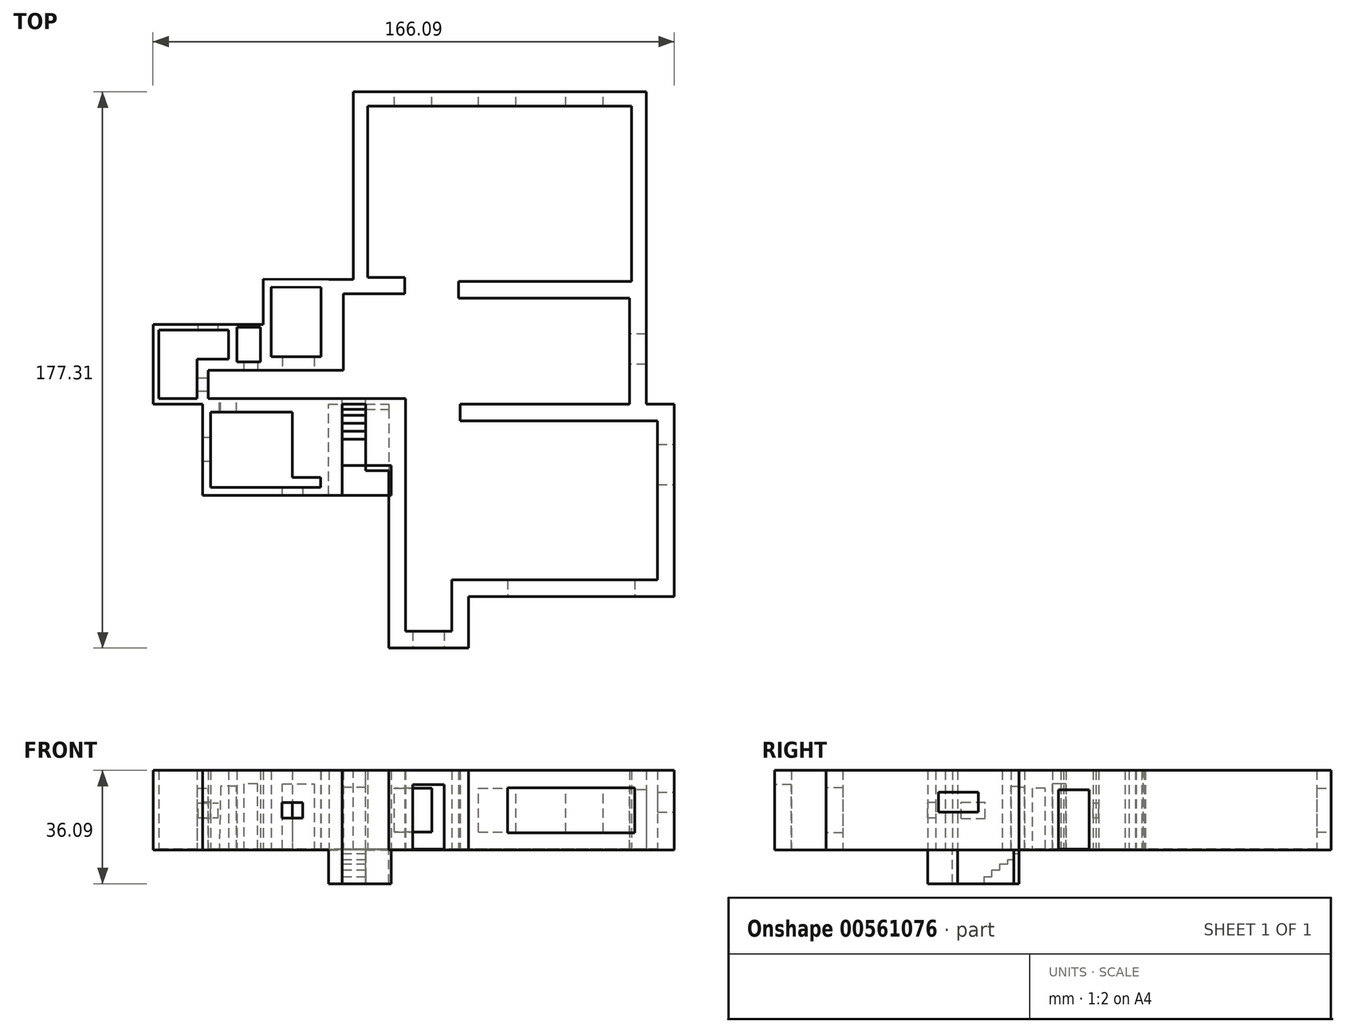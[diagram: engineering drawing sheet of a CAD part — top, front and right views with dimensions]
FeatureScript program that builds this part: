
annotation { "Feature Type Name" : "Feature", "Feature Type Description" : "" }
export const myFeature = defineFeature(function(context is Context, id is Id, definition is map)
    precondition{}
    {
        {
            var Q0;
            Q0=qCreatedBy(makeId("Top.planeOp"),FACE);
            var sketch = newSketch(context, id + "F0", { "sketchPlane" : qUnion([Q0])});
            skLineSegment(sketch, "E0", {"start": v(7.67, -76.15) * mm, "end": v(7.67, -59.75) * mm});
            skLineSegment(sketch, "E1", {"start": v(7.67, -59.75) * mm, "end": v(73.28, -59.75) * mm});
            skLineSegment(sketch, "E2", {"start": v(73.28, -59.75) * mm, "end": v(73.28, 1.64) * mm});
            skLineSegment(sketch, "E3", {"start": v(73.28, 1.64) * mm, "end": v(5.02, 1.64) * mm});
            skLineSegment(sketch, "E4", {"start": v(64.29, 9.05) * mm, "end": v(64.29, 21.75) * mm});
            skLineSegment(sketch, "E5", {"start": v(64.29, 21.75) * mm, "end": v(64.29, 30.21) * mm});
            skLineSegment(sketch, "E6", {"start": v(64.29, 30.21) * mm, "end": v(64.29, 40.8) * mm});
            skLineSegment(sketch, "E7", {"start": v(64.29, 40.8) * mm, "end": v(4.5, 40.8) * mm});
            skLineSegment(sketch, "E8", {"start": v(64.29, 51.38) * mm, "end": v(64.29, 56.89) * mm});
            skLineSegment(sketch, "E9", {"start": v(64.29, 56.89) * mm, "end": v(64.29, 101.16) * mm});
            skLineSegment(sketch, "E10", {"start": v(64.29, 101.16) * mm, "end": v(-28.95, 101.16) * mm});
            skLineSegment(sketch, "E11", {"start": v(-28.95, 101.16) * mm, "end": v(-28.95, 52.66) * mm});
            skLineSegment(sketch, "E12", {"start": v(-28.95, 52.66) * mm, "end": v(-17.16, 52.66) * mm});
            skLineSegment(sketch, "E13", {"start": v(-17.16, 52.66) * mm, "end": v(-17.16, 41.31) * mm});
            skLineSegment(sketch, "E14", {"start": v(-17.16, 41.31) * mm, "end": v(-36.74, 41.31) * mm});
            skLineSegment(sketch, "E15", {"start": v(-36.74, 41.31) * mm, "end": v(-36.74, 14.17) * mm});
            skLineSegment(sketch, "E16", {"start": v(-36.74, 14.17) * mm, "end": v(-42.75, 14.17) * mm});
            skLineSegment(sketch, "E17", {"start": v(-50.53, 14.17) * mm, "end": v(-57.65, 14.17) * mm});
            skLineSegment(sketch, "E18", {"start": v(-57.65, 14.17) * mm, "end": v(-57.65, 27.07) * mm});
            skLineSegment(sketch, "E19", {"start": v(-57.65, 41.54) * mm, "end": v(-36.74, 41.31) * mm});
            skLineSegment(sketch, "E20", {"start": v(-67, 14.17) * mm, "end": v(-67, 27.07) * mm});
            skLineSegment(sketch, "E21", {"start": v(-67, 27.07) * mm, "end": v(-57.65, 27.07) * mm});
            skPoint(sketch, "E22.start.orphan", {"position": v(-17.73, -76.15) * mm});
            skLineSegment(sketch, "E23", {"start": v(-17.73, -76.15) * mm, "end": v(-17.73, 1.64) * mm});
            skLineSegment(sketch, "E24", {"start": v(-17.73, 1.64) * mm, "end": v(-30.5, 1.64) * mm});
            skLineSegment(sketch, "E25", {"start": v(-39.19, 1.64) * mm, "end": v(-45.86, 1.64) * mm});
            skLineSegment(sketch, "E26", {"start": v(-45.86, -27.43) * mm, "end": v(-77, -27.43) * mm});
            skLineSegment(sketch, "E27", {"start": v(-77, -27.43) * mm, "end": v(-77, 1.64) * mm});
            skLineSegment(sketch, "E28", {"start": v(-77, 1.64) * mm, "end": v(-51.87, 1.64) * mm});
            skLineSegment(sketch, "E29", {"start": v(-77, 14.17) * mm, "end": v(-67, 14.17) * mm});
            skLineSegment(sketch, "E30", {"start": v(-77, 1.64) * mm, "end": v(-92.8, 1.64) * mm});
            skLineSegment(sketch, "E31", {"start": v(-92.8, 1.64) * mm, "end": v(-92.8, 27.07) * mm});
            skLineSegment(sketch, "E32", {"start": v(-77, 27.07) * mm, "end": v(-67, 27.07) * mm});
            skLineSegment(sketch, "E33", {"start": v(-77, 1.64) * mm, "end": v(-77, 8.77) * mm});
            skLineSegment(sketch, "E34", {"start": v(-45.86, -19.24) * mm, "end": v(-45.86, 1.64) * mm});
            skLineSegment(sketch, "E35", {"start": v(-45.86, -27.43) * mm, "end": v(-36.9, -27.43) * mm});
            skLineSegment(sketch, "E36", {"start": v(-36.9, -27.43) * mm, "end": v(-36.9, -19.24) * mm});
            skLineSegment(sketch, "E37", {"start": v(-36.9, -19.24) * mm, "end": v(-45.86, -19.24) * mm});
            skLineSegment(sketch, "E38", {"start": v(-67, 14.17) * mm, "end": v(-57.65, 14.17) * mm});
            skLineSegment(sketch, "E39", {"start": v(-77, 8.77) * mm, "end": v(-77, 14.17) * mm});
            skLineSegment(sketch, "E40", {"start": v(-51.87, 1.64) * mm, "end": v(-45.86, 1.64) * mm});
            skLineSegment(sketch, "E41", {"start": v(-50.53, 14.17) * mm, "end": v(-42.75, 14.17) * mm});
            skLineSegment(sketch, "E42", {"start": v(-39.19, 1.64) * mm, "end": v(-30.5, 1.64) * mm});
            skLineSegment(sketch, "E43", {"start": v(-17.73, -76.15) * mm, "end": v(7.67, -76.15) * mm});
            skLineSegment(sketch, "E44", {"start": v(64.29, 9.05) * mm, "end": v(64.29, 1.64) * mm});
            skLineSegment(sketch, "E45", {"start": v(64.29, 51.38) * mm, "end": v(64.29, 40.8) * mm});
            skLineSegment(sketch, "E46.0", {"start": v(67.95, -3.7) * mm, "end": v(5.02, -3.7) * mm});
            skLineSegment(sketch, "E46.1", {"start": v(67.95, -54.41) * mm, "end": v(67.95, -3.7) * mm});
            skLineSegment(sketch, "E46.2", {"start": v(2.33, -54.41) * mm, "end": v(67.95, -54.41) * mm});
            skLineSegment(sketch, "E46.3", {"start": v(2.33, -76.15) * mm, "end": v(2.33, -54.41) * mm});
            skLineSegment(sketch, "E47", {"start": v(5.02, -3.7) * mm, "end": v(5.02, 1.64) * mm});
            skLineSegment(sketch, "E48.0", {"start": v(58.95, 35.46) * mm, "end": v(4.5, 35.46) * mm});
            skLineSegment(sketch, "E48.1", {"start": v(58.95, 9.05) * mm, "end": v(58.95, 1.64) * mm});
            skLineSegment(sketch, "E48.2", {"start": v(58.95, 9.05) * mm, "end": v(58.95, 21.75) * mm});
            skLineSegment(sketch, "E48.3", {"start": v(58.95, 21.75) * mm, "end": v(58.95, 30.21) * mm});
            skLineSegment(sketch, "E48.4", {"start": v(58.95, 30.21) * mm, "end": v(58.95, 35.46) * mm});
            skLineSegment(sketch, "E49", {"start": v(4.5, 35.46) * mm, "end": v(4.5, 40.8) * mm});
            skLineSegment(sketch, "E50.0", {"start": v(59.72, 51.38) * mm, "end": v(59.72, 40.8) * mm});
            skLineSegment(sketch, "E50.1", {"start": v(59.72, 51.38) * mm, "end": v(59.72, 56.89) * mm});
            skLineSegment(sketch, "E50.2", {"start": v(59.72, 56.89) * mm, "end": v(59.72, 96.6) * mm});
            skLineSegment(sketch, "E50.3", {"start": v(59.72, 96.6) * mm, "end": v(-24.38, 96.6) * mm});
            skLineSegment(sketch, "E50.4", {"start": v(-24.38, 96.6) * mm, "end": v(-24.38, 57.23) * mm});
            skLineSegment(sketch, "E50.5", {"start": v(-32.17, 36.74) * mm, "end": v(-32.17, 14.17) * mm});
            skLineSegment(sketch, "E50.6", {"start": v(-12.59, 36.74) * mm, "end": v(-32.17, 36.74) * mm});
            skLineSegment(sketch, "E50.7", {"start": v(-12.59, 57.23) * mm, "end": v(-12.59, 36.74) * mm});
            skLineSegment(sketch, "E50.8", {"start": v(-24.38, 57.23) * mm, "end": v(-12.59, 57.23) * mm});
            skLineSegment(sketch, "E51", {"start": v(-32.17, 14.17) * mm, "end": v(-36.74, 14.17) * mm});
            skLineSegment(sketch, "E52.0", {"start": v(-50.53, 16.71) * mm, "end": v(-55.11, 16.71) * mm});
            skLineSegment(sketch, "E52.1", {"start": v(-55.11, 38.97) * mm, "end": v(-39.28, 38.8) * mm});
            skLineSegment(sketch, "E52.2", {"start": v(-39.28, 38.8) * mm, "end": v(-39.28, 16.71) * mm});
            skLineSegment(sketch, "E52.3", {"start": v(-55.11, 16.71) * mm, "end": v(-55.11, 38.97) * mm});
            skLineSegment(sketch, "E52.4", {"start": v(-39.28, 16.71) * mm, "end": v(-42.75, 16.71) * mm});
            skLineSegment(sketch, "E52.5", {"start": v(-50.53, 16.71) * mm, "end": v(-42.75, 16.71) * mm});
            skLineSegment(sketch, "E53.0", {"start": v(-66.1, 26.19) * mm, "end": v(-58.54, 26.19) * mm});
            skLineSegment(sketch, "E53.1", {"start": v(-66.1, 15.06) * mm, "end": v(-66.1, 26.19) * mm});
            skLineSegment(sketch, "E53.2", {"start": v(-66.1, 15.06) * mm, "end": v(-58.54, 15.06) * mm});
            skLineSegment(sketch, "E53.3", {"start": v(-58.54, 15.06) * mm, "end": v(-58.54, 26.19) * mm});
            skLineSegment(sketch, "E54", {"start": v(-92.8, 27.07) * mm, "end": v(-77, 27.07) * mm});
            skLineSegment(sketch, "E55.0", {"start": v(-78.79, 8.77) * mm, "end": v(-78.79, 15.95) * mm});
            skLineSegment(sketch, "E55.1", {"start": v(-78.79, 3.41) * mm, "end": v(-78.79, 8.77) * mm});
            skLineSegment(sketch, "E55.2", {"start": v(-78.79, 15.95) * mm, "end": v(-68.77, 15.95) * mm});
            skLineSegment(sketch, "E55.3", {"start": v(-78.79, 3.41) * mm, "end": v(-91.03, 3.41) * mm});
            skLineSegment(sketch, "E55.4", {"start": v(-68.77, 15.95) * mm, "end": v(-68.77, 25.3) * mm});
            skLineSegment(sketch, "E55.5", {"start": v(-77, 25.3) * mm, "end": v(-68.77, 25.3) * mm});
            skLineSegment(sketch, "E55.6", {"start": v(-91.03, 25.3) * mm, "end": v(-77, 25.3) * mm});
            skLineSegment(sketch, "E55.7", {"start": v(-91.03, 3.41) * mm, "end": v(-91.03, 25.3) * mm});
            skLineSegment(sketch, "E56.0", {"start": v(-17.73, 3.41) * mm, "end": v(-30.5, 3.41) * mm});
            skLineSegment(sketch, "E56.1", {"start": v(-39.19, 3.41) * mm, "end": v(-30.5, 3.41) * mm});
            skLineSegment(sketch, "E56.2", {"start": v(-39.19, 3.41) * mm, "end": v(-45.86, 3.41) * mm});
            skLineSegment(sketch, "E56.3", {"start": v(-50.53, 12.4) * mm, "end": v(-57.65, 12.4) * mm});
            skLineSegment(sketch, "E56.4", {"start": v(-50.53, 12.4) * mm, "end": v(-42.75, 12.4) * mm});
            skLineSegment(sketch, "E56.5", {"start": v(-36.74, 12.4) * mm, "end": v(-42.75, 12.4) * mm});
            skLineSegment(sketch, "E56.6", {"start": v(-32.17, 12.4) * mm, "end": v(-36.74, 12.4) * mm});
            skLineSegment(sketch, "E56.7", {"start": v(-67, 12.4) * mm, "end": v(-57.65, 12.4) * mm});
            skLineSegment(sketch, "E56.8", {"start": v(-75.23, 12.4) * mm, "end": v(-67, 12.4) * mm});
            skLineSegment(sketch, "E56.9", {"start": v(-75.23, 8.77) * mm, "end": v(-75.23, 12.4) * mm});
            skLineSegment(sketch, "E56.10", {"start": v(-75.23, 3.41) * mm, "end": v(-75.23, 8.77) * mm});
            skLineSegment(sketch, "E56.11", {"start": v(-75.23, 3.41) * mm, "end": v(-51.87, 3.41) * mm});
            skLineSegment(sketch, "E56.12", {"start": v(-51.87, 3.41) * mm, "end": v(-45.86, 3.41) * mm});
            skLineSegment(sketch, "E57", {"start": v(-17.73, 1.64) * mm, "end": v(-17.73, 3.41) * mm});
            skLineSegment(sketch, "E58.0", {"start": v(-39.43, -21.78) * mm, "end": v(-48.4, -21.78) * mm});
            skLineSegment(sketch, "E58.1", {"start": v(-39.43, -24.9) * mm, "end": v(-39.43, -21.78) * mm});
            skLineSegment(sketch, "E58.2", {"start": v(-48.4, -21.78) * mm, "end": v(-48.4, -0.9) * mm});
            skLineSegment(sketch, "E58.3", {"start": v(-45.86, -24.9) * mm, "end": v(-39.43, -24.9) * mm});
            skLineSegment(sketch, "E58.4", {"start": v(-51.87, -0.9) * mm, "end": v(-48.4, -0.9) * mm});
            skLineSegment(sketch, "E58.5", {"start": v(-74.47, -0.9) * mm, "end": v(-51.87, -0.9) * mm});
            skLineSegment(sketch, "E58.6", {"start": v(-74.47, -24.9) * mm, "end": v(-74.47, -0.9) * mm});
            skLineSegment(sketch, "E58.7", {"start": v(-45.86, -24.9) * mm, "end": v(-74.47, -24.9) * mm});
            skLineSegment(sketch, "E59", {"start": v(-57.65, 41.54) * mm, "end": v(-57.65, 27.07) * mm});
            skLineSegment(sketch, "E60", {"start": v(-32.17, 12.4) * mm, "end": v(-32.17, 14.17) * mm});
            skLineSegment(sketch, "E61.0", {"start": v(-12.4, -76.15) * mm, "end": v(-12.4, 1.64) * mm});
            skLineSegment(sketch, "E62", {"start": v(-12.4, 1.64) * mm, "end": v(-17.73, 1.64) * mm});
            skLineSegment(sketch, "E63", {"start": v(-17.73, 3.41) * mm, "end": v(-12.4, 3.41) * mm});
            skLineSegment(sketch, "E64", {"start": v(-12.4, 3.41) * mm, "end": v(-12.4, 1.64) * mm});
            skLineSegment(sketch, "E65.0", {"start": v(-17.73, -70.82) * mm, "end": v(7.67, -70.82) * mm});
            skSolve(sketch);
        }
        {
            var Q0;
            {var subQ4=sQuery(id+"F0.wireOp",EDGE,"E0");Q0=makeQuery(id+"F0.imprint","IMPRINT",FACE,{"disambiguationData":[TD([[makeQuery(id+"F0.imprint","IMPRINT",EDGE,{"derivedFrom":subQ4}),1.0]])]});}
            var Q1;
            {var subQ0=sQuery(id+"F0.wireOp",EDGE,"E23");Q1=makeQuery(id+"F0.imprint","IMPRINT",FACE,{"disambiguationData":[TD([[makeQuery(id+"F0.imprint","IMPRINT",EDGE,{"derivedFrom":subQ0}),-1.0]])]});}
            var Q2;
            Q2=makeQuery(id+"F0.imprint","IMPRINT",FACE,{"disambiguationData":[TD([[makeQuery(id+"F0.imprint","IMPRINT",EDGE,{"derivedFrom":sQuery(id+"F0.wireOp",EDGE,"E26")}),-1.0]])]});
            var Q3;
            Q3=makeQuery(id+"F0.imprint","IMPRINT",FACE,{"disambiguationData":[TD([[makeQuery(id+"F0.imprint","IMPRINT",EDGE,{"derivedFrom":sQuery(id+"F0.wireOp",EDGE,"E4")}),1.0]])]});
            var Q4;
            Q4=makeQuery(id+"F0.imprint","IMPRINT",FACE,{"disambiguationData":[TD([[makeQuery(id+"F0.imprint","IMPRINT",EDGE,{"derivedFrom":sQuery(id+"F0.wireOp",EDGE,"E20")}),1.0]])]});
            var Q5;
            Q5=makeQuery(id+"F0.imprint","IMPRINT",FACE,{"disambiguationData":[TD([[makeQuery(id+"F0.imprint","IMPRINT",EDGE,{"derivedFrom":sQuery(id+"F0.wireOp",EDGE,"E57")}),-1.0]])]});
            var Q6;
            Q6=makeQuery(id+"F0.imprint","IMPRINT",FACE,{"disambiguationData":[TD([[makeQuery(id+"F0.imprint","IMPRINT",EDGE,{"derivedFrom":sQuery(id+"F0.wireOp",EDGE,"E8")}),1.0]])]});
            var Q7;
            Q7=makeQuery(id+"F0.imprint","IMPRINT",FACE,{"disambiguationData":[TD([[makeQuery(id+"F0.imprint","IMPRINT",EDGE,{"derivedFrom":sQuery(id+"F0.wireOp",EDGE,"E15")}),-1.0]])]});
            var Q8;
            Q8=makeQuery(id+"F0.imprint","IMPRINT",FACE,{"disambiguationData":[TD([[makeQuery(id+"F0.imprint","IMPRINT",EDGE,{"derivedFrom":sQuery(id+"F0.wireOp",EDGE,"E18")}),1.0]])]});
            var Q9;
            Q9=makeQuery(id+"F0.imprint","IMPRINT",FACE,{"disambiguationData":[TD([[makeQuery(id+"F0.imprint","IMPRINT",EDGE,{"derivedFrom":sQuery(id+"F0.wireOp",EDGE,"E16")}),1.0]])]});
            var Q10;
            {var subQ8=sQuery(id+"F0.wireOp",EDGE,"E1");Q10=makeQuery(id+"F0.imprint","IMPRINT",FACE,{"disambiguationData":[TD([[makeQuery(id+"F0.imprint","IMPRINT",EDGE,{"derivedFrom":subQ8}),1.0]])]});}
            var Q11;
            {var subQ0=sQuery(id+"F0.wireOp",EDGE,"E46.3");var subQ1=sQuery(id+"F0.wireOp",EDGE,"E43");var subQ2=makeQuery(id+"F0.imprint","INTERSECT",VERTEX,{"derivedFrom":[subQ1,subQ0]});Q11=makeQuery(id+"F0.imprint","IMPRINT",FACE,{"disambiguationData":[TD([[makeQuery(id+"F0.imprint","IMPRINT",EDGE,{"disambiguationData":[TD([[subQ2,1.0]])],"derivedFrom":subQ1}),1.0]])]});}
            extrude(context, id + "F1", {"entities" : qUnion([Q0, Q1, Q2, Q3, Q4, Q5, Q6, Q7, Q8, Q9, Q10, Q11]), "depth" : 25.4 * mm, "offsetDistance" : 25.4 * mm});
        }
        {
            var Q0;
            Q0=makeQuery(id+"F0.imprint","IMPRINT",FACE,{"disambiguationData":[TD([[makeQuery(id+"F0.imprint","IMPRINT",EDGE,{"derivedFrom":sQuery(id+"F0.wireOp",EDGE,"E46.0")}),1.0]])]});
            var Q1;
            Q1=makeQuery(id+"F0.imprint","IMPRINT",FACE,{"disambiguationData":[TD([[makeQuery(id+"F0.imprint","IMPRINT",EDGE,{"derivedFrom":sQuery(id+"F0.wireOp",EDGE,"E52.0")}),-1.0]])]});
            var Q2;
            Q2=makeQuery(id+"F0.imprint","IMPRINT",FACE,{"disambiguationData":[TD([[makeQuery(id+"F0.imprint","IMPRINT",EDGE,{"derivedFrom":sQuery(id+"F0.wireOp",EDGE,"E53.0")}),-1.0]])]});
            var Q3;
            Q3=makeQuery(id+"F0.imprint","IMPRINT",FACE,{"disambiguationData":[TD([[makeQuery(id+"F0.imprint","IMPRINT",EDGE,{"derivedFrom":sQuery(id+"F0.wireOp",EDGE,"E55.0")}),1.0]])]});
            var Q4;
            Q4=makeQuery(id+"F0.imprint","IMPRINT",FACE,{"disambiguationData":[TD([[makeQuery(id+"F0.imprint","IMPRINT",EDGE,{"derivedFrom":sQuery(id+"F0.wireOp",EDGE,"E58.0")}),1.0]])]});
            extrude(context, id + "F2", {"entities" : qUnion([Q0, Q1, Q2, Q3, Q4]), "operationType" : NewBodyOperationType.ADD, "depth" : 0.25 * mm, "offsetDistance" : 25.4 * mm});
        }
        {
            var Q0;
            Q0=makeQuery(id+"F1.opExtrude","SWEPT_FACE",FACE,{"disambiguationData":[OSD([sQuery(id+"F0.wireOp",EDGE,"E43")])]});
            var sketch = newSketch(context, id + "F3", { "sketchPlane" : qUnion([Q0])});
            skLineSegment(sketch, "E66", {"start": v(-5.03, 0) * mm, "end": v(-5.03, 25.4) * mm});
            skLineSegment(sketch, "E67", {"start": v(-10.06, 0) * mm, "end": v(-10.06, 20.86) * mm});
            skLineSegment(sketch, "E68", {"start": v(-10.06, 20.86) * mm, "end": v(-5.03, 20.86) * mm});
            skLineSegment(sketch, "E69", {"start": v(-5.03, 20.86) * mm, "end": v(0, 20.86) * mm});
            skLineSegment(sketch, "E70", {"start": v(0, 20.86) * mm, "end": v(0, 0) * mm});
            skSolve(sketch);
        }
        {
            var Q0;
            Q0 = qSketchRegion(id + "F3", true);
            var Q1;
            {var subQ4=sQuery(id+"F3.wireOp",EDGE,"E67");Q1=makeQuery(id+"F3.imprint","IMPRINT",FACE,{"disambiguationData":[TD([[makeQuery(id+"F3.imprint","IMPRINT",EDGE,{"derivedFrom":subQ4}),-1.0]])]});}
            var Q2;
            {var subQ3=sQuery(id+"F3.wireOp",EDGE,"E69");Q2=makeQuery(id+"F3.imprint","IMPRINT",FACE,{"disambiguationData":[TD([[makeQuery(id+"F3.imprint","IMPRINT",EDGE,{"derivedFrom":subQ3}),-1.0]])]});}
            extrude(context, id + "F4", {"entities" : qUnion([Q0, Q1, Q2]), "operationType" : NewBodyOperationType.REMOVE, "oppositeDirection" : true, "depth" : 5.33 * mm, "offsetDistance" : 25.4 * mm});
        }
        {
            var Q0;
            Q0=makeQuery(id+"F1.opExtrude","SWEPT_FACE",FACE,{"disambiguationData":[OSD([sQuery(id+"F0.wireOp",EDGE,"E48.1"),sQuery(id+"F0.wireOp",EDGE,"E48.2"),sQuery(id+"F0.wireOp",EDGE,"E48.3"),sQuery(id+"F0.wireOp",EDGE,"E48.4")])]});
            var sketch = newSketch(context, id + "F5", { "sketchPlane" : qUnion([Q0])});
            skLineSegment(sketch, "E71", {"start": v(-24.02, 0.25) * mm, "end": v(-24.02, 19.18) * mm});
            skLineSegment(sketch, "E72", {"start": v(-24.02, 19.18) * mm, "end": v(-14.28, 19.18) * mm});
            skLineSegment(sketch, "E73", {"start": v(-14.28, 19.18) * mm, "end": v(-14.28, 0) * mm});
            skSolve(sketch);
        }
        {
            var Q0;
            Q0 = qSketchRegion(id + "F5", true);
            var Q1;
            {var subQ0=sQuery(id+"F5.wireOp",EDGE,"E71");Q1=makeQuery(id+"F5.imprint","IMPRINT",FACE,{"disambiguationData":[TD([[makeQuery(id+"F5.imprint","IMPRINT",EDGE,{"derivedFrom":subQ0}),-1.0]])]});}
            extrude(context, id + "F6", {"entities" : qUnion([Q0, Q1]), "operationType" : NewBodyOperationType.REMOVE, "oppositeDirection" : true, "depth" : 25.4 * mm, "offsetDistance" : 25.4 * mm});
        }
        {
            var Q0;
            Q0=makeQuery(id+"F1.opExtrude","SWEPT_FACE",FACE,{"disambiguationData":[OSD([sQuery(id+"F0.wireOp",EDGE,"E56.3"),sQuery(id+"F0.wireOp",EDGE,"E56.4"),sQuery(id+"F0.wireOp",EDGE,"E56.5"),sQuery(id+"F0.wireOp",EDGE,"E56.6"),sQuery(id+"F0.wireOp",EDGE,"E56.7"),sQuery(id+"F0.wireOp",EDGE,"E56.8")])]});
            var sketch = newSketch(context, id + "F7", { "sketchPlane" : qUnion([Q0])});
            skLineSegment(sketch, "E74", {"start": v(-51.57, 0.25) * mm, "end": v(-51.57, 21.1) * mm});
            skLineSegment(sketch, "E75", {"start": v(-51.57, 21.1) * mm, "end": v(-41.46, 21.1) * mm});
            skLineSegment(sketch, "E76", {"start": v(-41.46, 21.1) * mm, "end": v(-41.46, 0) * mm});
            skLineSegment(sketch, "E77", {"start": v(-63.97, 0.25) * mm, "end": v(-63.97, 21.1) * mm});
            skLineSegment(sketch, "E78", {"start": v(-63.97, 21.1) * mm, "end": v(-59.47, 21.1) * mm});
            skLineSegment(sketch, "E79", {"start": v(-59.47, 21.1) * mm, "end": v(-59.47, 0) * mm});
            skSolve(sketch);
        }
        {
            var Q0;
            Q0 = qSketchRegion(id + "F7", true);
            var Q1;
            {var subQ0=sQuery(id+"F7.wireOp",EDGE,"E74");Q1=makeQuery(id+"F7.imprint","IMPRINT",FACE,{"disambiguationData":[TD([[makeQuery(id+"F7.imprint","IMPRINT",EDGE,{"derivedFrom":subQ0}),-1.0]])]});}
            var Q2;
            {var subQ0=sQuery(id+"F7.wireOp",EDGE,"E77");Q2=makeQuery(id+"F7.imprint","IMPRINT",FACE,{"disambiguationData":[TD([[makeQuery(id+"F7.imprint","IMPRINT",EDGE,{"derivedFrom":subQ0}),-1.0]])]});}
            extrude(context, id + "F8", {"entities" : qUnion([Q0, Q1, Q2]), "operationType" : NewBodyOperationType.REMOVE, "oppositeDirection" : true, "depth" : 12.55 * mm, "offsetDistance" : 25.4 * mm});
        }
        {
            var Q0;
            Q0=makeQuery(id+"F1.opExtrude","SWEPT_FACE",FACE,{"disambiguationData":[OSD([sQuery(id+"F0.wireOp",EDGE,"E56.9"),sQuery(id+"F0.wireOp",EDGE,"E56.10")])]});
            var sketch = newSketch(context, id + "F9", { "sketchPlane" : qUnion([Q0])});
            skLineSegment(sketch, "E80", {"start": v(5.84, 0.25) * mm, "end": v(5.84, 19.77) * mm});
            skLineSegment(sketch, "E81", {"start": v(5.84, 19.77) * mm, "end": v(10.06, 19.77) * mm});
            skLineSegment(sketch, "E82", {"start": v(10.06, 19.77) * mm, "end": v(10.06, 0.25) * mm});
            skSolve(sketch);
        }
        {
            var Q0;
            Q0 = qSketchRegion(id + "F9", true);
            var Q1;
            {var subQ0=sQuery(id+"F9.wireOp",EDGE,"E80");Q1=makeQuery(id+"F9.imprint","IMPRINT",FACE,{"disambiguationData":[TD([[makeQuery(id+"F9.imprint","IMPRINT",EDGE,{"derivedFrom":subQ0}),-1.0]])]});}
            extrude(context, id + "F10", {"entities" : qUnion([Q0, Q1]), "operationType" : NewBodyOperationType.REMOVE, "oppositeDirection" : true, "depth" : 8.38 * mm, "offsetDistance" : 25.4 * mm});
        }
        {
            var Q0;
            Q0=makeQuery(id+"F1.opExtrude","SWEPT_FACE",FACE,{"disambiguationData":[OSD([sQuery(id+"F0.wireOp",EDGE,"E56.0"),sQuery(id+"F0.wireOp",EDGE,"E56.1"),sQuery(id+"F0.wireOp",EDGE,"E56.2"),sQuery(id+"F0.wireOp",EDGE,"E56.11"),sQuery(id+"F0.wireOp",EDGE,"E56.12"),sQuery(id+"F0.wireOp",EDGE,"E63")])]});
            var sketch = newSketch(context, id + "F11", { "sketchPlane" : qUnion([Q0])});
            skLineSegment(sketch, "E83", {"start": v(66.17, 0.25) * mm, "end": v(66.17, 20.44) * mm});
            skLineSegment(sketch, "E84", {"start": v(66.17, 20.44) * mm, "end": v(71.24, 20.44) * mm});
            skLineSegment(sketch, "E85", {"start": v(71.24, 20.44) * mm, "end": v(71.71, 0.25) * mm});
            skSolve(sketch);
        }
        {
            var Q0;
            Q0 = qSketchRegion(id + "F11", true);
            var Q1;
            {var subQ0=sQuery(id+"F11.wireOp",EDGE,"E83");Q1=makeQuery(id+"F11.imprint","IMPRINT",FACE,{"disambiguationData":[TD([[makeQuery(id+"F11.imprint","IMPRINT",EDGE,{"derivedFrom":subQ0}),-1.0]])]});}
            extrude(context, id + "F12", {"entities" : qUnion([Q0, Q1]), "operationType" : NewBodyOperationType.REMOVE, "oppositeDirection" : true, "depth" : 14.78 * mm, "offsetDistance" : 25.4 * mm});
        }
        {
            var Q0;
            Q0=makeQuery(id+"F1.opExtrude","SWEPT_FACE",FACE,{"disambiguationData":[OSD([sQuery(id+"F0.wireOp",EDGE,"E56.0"),sQuery(id+"F0.wireOp",EDGE,"E56.1"),sQuery(id+"F0.wireOp",EDGE,"E56.2"),sQuery(id+"F0.wireOp",EDGE,"E56.11"),sQuery(id+"F0.wireOp",EDGE,"E56.12"),sQuery(id+"F0.wireOp",EDGE,"E63")])]});
            var sketch = newSketch(context, id + "F13", { "sketchPlane" : qUnion([Q0])});
            skLineSegment(sketch, "E86", {"start": v(25.02, 0.25) * mm, "end": v(25.02, 20.13) * mm});
            skLineSegment(sketch, "E87", {"start": v(25.02, 20.13) * mm, "end": v(32.53, 20.13) * mm});
            skLineSegment(sketch, "E88", {"start": v(32.53, 20.13) * mm, "end": v(32.53, 0.25) * mm});
            skSolve(sketch);
        }
        {
            var Q0;
            Q0 = qSketchRegion(id + "F13", true);
            var Q1;
            {var subQ0=sQuery(id+"F13.wireOp",EDGE,"E86");Q1=makeQuery(id+"F13.imprint","IMPRINT",FACE,{"disambiguationData":[TD([[makeQuery(id+"F13.imprint","IMPRINT",EDGE,{"derivedFrom":subQ0}),-1.0]])]});}
            extrude(context, id + "F14", {"entities" : qUnion([Q0, Q1]), "operationType" : NewBodyOperationType.REMOVE, "oppositeDirection" : true, "depth" : 25.4 * mm, "offsetDistance" : 25.4 * mm});
        }
        {
            var Q0;
            Q0=makeQuery(id+"F1.opExtrude","SWEPT_FACE",FACE,{"disambiguationData":[OSD([sQuery(id+"F0.wireOp",EDGE,"E26"),sQuery(id+"F0.wireOp",EDGE,"E35")])]});
            var sketch = newSketch(context, id + "F15", { "sketchPlane" : qUnion([Q0])});
            skLineSegment(sketch, "E89.bottom", {"start": v(-45.08, 10.22) * mm, "end": v(-51.7, 10.22) * mm});
            skLineSegment(sketch, "E89.top", {"start": v(-45.08, 15.18) * mm, "end": v(-51.7, 15.18) * mm});
            skLineSegment(sketch, "E89.left", {"start": v(-45.08, 10.22) * mm, "end": v(-45.08, 15.18) * mm});
            skLineSegment(sketch, "E89.right", {"start": v(-51.7, 10.22) * mm, "end": v(-51.7, 15.18) * mm});
            skPoint(sketch, "E89.middle", {"position": v(-48.38, 12.7) * mm});
            skPoint(sketch, "E89.middle.positionSnap0", {"position": v(-77, 12.7) * mm});
            skPoint(sketch, "E89.centerSnap0", {"position": v(-77, 12.7) * mm});
            skSolve(sketch);
        }
        {
            var Q0;
            Q0 = qSketchRegion(id + "F15", true);
            extrude(context, id + "F16", {"entities" : qUnion([Q0]), "operationType" : NewBodyOperationType.REMOVE, "oppositeDirection" : true, "depth" : 2.84 * mm, "offsetDistance" : 25.4 * mm});
        }
        {
            var Q0;
            Q0=makeQuery(id+"F1.opExtrude","SWEPT_FACE",FACE,{"disambiguationData":[OSD([sQuery(id+"F0.wireOp",EDGE,"E1")])]});
            var sketch = newSketch(context, id + "F17", { "sketchPlane" : qUnion([Q0])});
            skLineSegment(sketch, "E90.bottom", {"start": v(60.67, 5.57) * mm, "end": v(20.14, 5.57) * mm});
            skLineSegment(sketch, "E90.top", {"start": v(60.67, 19.83) * mm, "end": v(20.14, 19.83) * mm});
            skLineSegment(sketch, "E90.left", {"start": v(60.67, 5.57) * mm, "end": v(60.67, 19.83) * mm});
            skLineSegment(sketch, "E90.right", {"start": v(20.14, 5.57) * mm, "end": v(20.14, 19.83) * mm});
            skPoint(sketch, "E90.middle", {"position": v(40.4, 12.7) * mm});
            skPoint(sketch, "E90.middle.positionSnap0", {"position": v(7.67, 12.7) * mm});
            skPoint(sketch, "E90.centerSnap0", {"position": v(7.67, 12.7) * mm});
            skSolve(sketch);
        }
        {
            var Q0;
            Q0=makeQuery(id+"F17.imprint","IMPRINT",FACE,{"disambiguationData":[TD([[makeQuery(id+"F17.imprint","IMPRINT",EDGE,{"derivedFrom":sQuery(id+"F17.wireOp",EDGE,"E90.bottom")}),-1.0]])]});
            var Q1;
            Q1=sQuery(id+"F17.wireOp",EDGE,"E90.left");
            extrude(context, id + "F18", {"entities" : qUnion([Q0]), "operationType" : NewBodyOperationType.REMOVE, "surfaceEntities" : qUnion([Q1]), "oppositeDirection" : true, "depth" : 25.4 * mm, "offsetDistance" : 25.4 * mm});
        }
        {
            var Q0;
            Q0=makeQuery(id+"F1.opExtrude","SWEPT_FACE",FACE,{"disambiguationData":[OSD([sQuery(id+"F0.wireOp",EDGE,"E2")])]});
            var sketch = newSketch(context, id + "F19", { "sketchPlane" : qUnion([Q0])});
            skLineSegment(sketch, "E91.bottom", {"start": v(-11.25, 12.18) * mm, "end": v(-24.05, 12.18) * mm});
            skLineSegment(sketch, "E91.top", {"start": v(-11.25, 18.48) * mm, "end": v(-24.05, 18.48) * mm});
            skLineSegment(sketch, "E91.left", {"start": v(-11.25, 12.18) * mm, "end": v(-11.25, 18.48) * mm});
            skLineSegment(sketch, "E91.right", {"start": v(-24.05, 12.18) * mm, "end": v(-24.05, 18.48) * mm});
            skPoint(sketch, "E91.middle", {"position": v(-17.65, 15.33) * mm});
            skSolve(sketch);
        }
        {
            var Q0;
            Q0 = qSketchRegion(id + "F19", true);
            extrude(context, id + "F20", {"entities" : qUnion([Q0]), "operationType" : NewBodyOperationType.REMOVE, "oppositeDirection" : true, "depth" : 25.4 * mm, "offsetDistance" : 25.4 * mm});
        }
        {
            var Q0;
            Q0=makeQuery(id+"F1.opExtrude","SWEPT_FACE",FACE,{"disambiguationData":[OSD([sQuery(id+"F0.wireOp",EDGE,"E10")])]});
            var sketch = newSketch(context, id + "F21", { "sketchPlane" : qUnion([Q0])});
            skLineSegment(sketch, "E92.bottom", {"start": v(-38.68, 5.72) * mm, "end": v(-50.62, 5.72) * mm});
            skLineSegment(sketch, "E92.top", {"start": v(-38.68, 19.69) * mm, "end": v(-50.62, 19.69) * mm});
            skLineSegment(sketch, "E92.left", {"start": v(-38.68, 5.72) * mm, "end": v(-38.68, 19.69) * mm});
            skLineSegment(sketch, "E92.right", {"start": v(-50.62, 5.72) * mm, "end": v(-50.62, 19.69) * mm});
            skPoint(sketch, "E92.middle", {"position": v(-44.65, 12.7) * mm});
            skPoint(sketch, "E92.middle.positionSnap0", {"position": v(-64.29, 12.7) * mm});
            skPoint(sketch, "E92.centerSnap0", {"position": v(-64.29, 12.7) * mm});
            skLineSegment(sketch, "E93.bottom", {"start": v(-10.9, 5.72) * mm, "end": v(-22.83, 5.72) * mm});
            skLineSegment(sketch, "E93.top", {"start": v(-10.9, 19.69) * mm, "end": v(-22.83, 19.69) * mm});
            skLineSegment(sketch, "E93.left", {"start": v(-10.9, 5.72) * mm, "end": v(-10.9, 19.69) * mm});
            skLineSegment(sketch, "E93.right", {"start": v(-22.83, 5.72) * mm, "end": v(-22.83, 19.69) * mm});
            skPoint(sketch, "E93.middle", {"position": v(-16.86, 12.7) * mm});
            skPoint(sketch, "E93.middle.positionSnap0", {"position": v(-38.68, 12.7) * mm});
            skPoint(sketch, "E93.centerSnap0", {"position": v(-38.68, 12.7) * mm});
            skLineSegment(sketch, "E94.bottom", {"start": v(15.9, 5.72) * mm, "end": v(3.97, 5.72) * mm});
            skLineSegment(sketch, "E94.top", {"start": v(15.9, 19.69) * mm, "end": v(3.97, 19.69) * mm});
            skLineSegment(sketch, "E94.left", {"start": v(15.9, 5.72) * mm, "end": v(15.9, 19.69) * mm});
            skLineSegment(sketch, "E94.right", {"start": v(3.97, 5.72) * mm, "end": v(3.97, 19.69) * mm});
            skPoint(sketch, "E94.middle", {"position": v(9.94, 12.7) * mm});
            skPoint(sketch, "E94.middle.positionSnap0", {"position": v(-10.9, 12.7) * mm});
            skPoint(sketch, "E94.centerSnap0", {"position": v(-10.9, 12.7) * mm});
            skSolve(sketch);
        }
        {
            var Q0;
            Q0 = qSketchRegion(id + "F21", true);
            extrude(context, id + "F22", {"entities" : qUnion([Q0]), "operationType" : NewBodyOperationType.REMOVE, "oppositeDirection" : true, "depth" : 25.4 * mm, "offsetDistance" : 25.4 * mm});
        }
        {
            var Q0;
            Q0=makeQuery(id+"F1.opExtrude","SWEPT_FACE",FACE,{"disambiguationData":[OSD([sQuery(id+"F0.wireOp",EDGE,"E21"),sQuery(id+"F0.wireOp",EDGE,"E32"),sQuery(id+"F0.wireOp",EDGE,"E54")])]});
            var sketch = newSketch(context, id + "F23", { "sketchPlane" : qUnion([Q0])});
            skLineSegment(sketch, "E95.bottom", {"start": v(78.42, 10.32) * mm, "end": v(72.03, 10.32) * mm});
            skLineSegment(sketch, "E95.top", {"start": v(78.42, 15.08) * mm, "end": v(72.03, 15.08) * mm});
            skLineSegment(sketch, "E95.left", {"start": v(78.42, 10.32) * mm, "end": v(78.42, 15.08) * mm});
            skLineSegment(sketch, "E95.right", {"start": v(72.03, 10.32) * mm, "end": v(72.03, 15.08) * mm});
            skPoint(sketch, "E95.middle", {"position": v(75.23, 12.7) * mm});
            skPoint(sketch, "E95.middle.positionSnap0", {"position": v(57.65, 12.7) * mm});
            skPoint(sketch, "E95.middle.positionSnap1", {"position": v(75.23, 0) * mm});
            skPoint(sketch, "E95.centerSnap0", {"position": v(57.65, 12.7) * mm});
            skPoint(sketch, "E95.centerSnap1", {"position": v(75.23, 0) * mm});
            skSolve(sketch);
        }
        {
            var Q0;
            Q0 = qSketchRegion(id + "F23", true);
            extrude(context, id + "F24", {"entities" : qUnion([Q0]), "operationType" : NewBodyOperationType.REMOVE, "oppositeDirection" : true, "depth" : 5.18 * mm, "offsetDistance" : 25.4 * mm});
        }
        {
            var Q0;
            Q0=makeQuery(id+"F1.opExtrude","SWEPT_FACE",FACE,{"disambiguationData":[OSD([sQuery(id+"F0.wireOp",EDGE,"E27")])]});
            var sketch = newSketch(context, id + "F25", { "sketchPlane" : qUnion([Q0])});
            skLineSegment(sketch, "E96.bottom", {"start": v(16.7, 10.13) * mm, "end": v(9.1, 10.13) * mm});
            skLineSegment(sketch, "E96.top", {"start": v(16.7, 15.27) * mm, "end": v(9.1, 15.27) * mm});
            skLineSegment(sketch, "E96.left", {"start": v(16.7, 10.13) * mm, "end": v(16.7, 15.27) * mm});
            skLineSegment(sketch, "E96.right", {"start": v(9.1, 10.13) * mm, "end": v(9.1, 15.27) * mm});
            skPoint(sketch, "E96.middle", {"position": v(12.9, 12.7) * mm});
            skPoint(sketch, "E96.middle.positionSnap0", {"position": v(12.9, 0) * mm});
            skPoint(sketch, "E96.middle.positionSnap1", {"position": v(-1.64, 12.7) * mm});
            skPoint(sketch, "E96.centerSnap0", {"position": v(12.9, 0) * mm});
            skPoint(sketch, "E96.centerSnap1", {"position": v(-1.64, 12.7) * mm});
            skSolve(sketch);
        }
        {
            var Q0;
            Q0 = qSketchRegion(id + "F25", true);
            extrude(context, id + "F26", {"entities" : qUnion([Q0]), "operationType" : NewBodyOperationType.REMOVE, "oppositeDirection" : true, "depth" : 3.56 * mm, "offsetDistance" : 25.4 * mm});
        }
        {
            var Q0;
            Q0=makeQuery(id+"F1.opExtrude","SWEPT_FACE",FACE,{"disambiguationData":[OSD([sQuery(id+"F0.wireOp",EDGE,"E24"),sQuery(id+"F0.wireOp",EDGE,"E25"),sQuery(id+"F0.wireOp",EDGE,"E42")])]});
            var sketch = newSketch(context, id + "F27", { "sketchPlane" : qUnion([Q0])});
            skLineSegment(sketch, "E97", {"start": v(-32.53, 0.25) * mm, "end": v(-32.53, -10.68) * mm});
            skLineSegment(sketch, "E98", {"start": v(-25.02, 0.25) * mm, "end": v(-25.02, -10.68) * mm});
            skLineSegment(sketch, "E99", {"start": v(-32.53, -10.68) * mm, "end": v(-25.02, -10.68) * mm});
            skSolve(sketch);
        }
        {
            var Q0;
            Q0 = qSketchRegion(id + "F27", true);
            var Q1;
            {var subQ0=sQuery(id+"F27.wireOp",EDGE,"E99");Q1=makeQuery(id+"F27.imprint","IMPRINT",FACE,{"disambiguationData":[TD([[makeQuery(id+"F27.imprint","IMPRINT",EDGE,{"derivedFrom":subQ0}),1.0]])]});}
            extrude(context, id + "F28", {"entities" : qUnion([Q0, Q1]), "depth" : 11.18 * mm, "offsetDistance" : 25.4 * mm});
        }
        {
            var Q0;
            Q0=makeQuery(id+"F28.opExtrude","SWEPT_FACE",FACE,{"disambiguationData":[OSD([sQuery(id+"F27.wireOp",EDGE,"E98")])]});
            var sketch = newSketch(context, id + "F29", { "sketchPlane" : qUnion([Q0])});
            skLineSegment(sketch, "E100", {"start": v(-9.54, -10.68) * mm, "end": v(-9.54, -8.47) * mm});
            skLineSegment(sketch, "E101", {"start": v(-9.54, -8.47) * mm, "end": v(-7, -8.47) * mm});
            skLineSegment(sketch, "E102", {"start": v(-7, -8.47) * mm, "end": v(-7, -6.34) * mm});
            skLineSegment(sketch, "E103", {"start": v(-7, -6.34) * mm, "end": v(-4.46, -6.34) * mm});
            skLineSegment(sketch, "E104", {"start": v(-4.46, -6.34) * mm, "end": v(-4.46, -4.43) * mm});
            skLineSegment(sketch, "E105", {"start": v(-4.46, -4.43) * mm, "end": v(-1.92, -4.43) * mm});
            skLineSegment(sketch, "E106", {"start": v(-1.92, -4.43) * mm, "end": v(-1.92, -2.98) * mm});
            skLineSegment(sketch, "E107", {"start": v(-1.92, -2.98) * mm, "end": v(0, -2.98) * mm});
            skLineSegment(sketch, "E108", {"start": v(0, -2.98) * mm, "end": v(0, -1.06) * mm});
            skLineSegment(sketch, "E109", {"start": v(0, -1.06) * mm, "end": v(1.64, -1.06) * mm});
            skLineSegment(sketch, "E110", {"start": v(1.64, -1.06) * mm, "end": v(1.64, 0) * mm});
            skSolve(sketch);
        }
        {
            var Q0;
            Q0 = qSketchRegion(id + "F29", true);
            var Q1;
            {var subQ0=sQuery(id+"F29.wireOp",EDGE,"E101");Q1=makeQuery(id+"F29.imprint","IMPRINT",FACE,{"disambiguationData":[TD([[makeQuery(id+"F29.imprint","IMPRINT",EDGE,{"derivedFrom":subQ0}),1.0]])]});}
            extrude(context, id + "F30", {"entities" : qUnion([Q0, Q1]), "operationType" : NewBodyOperationType.REMOVE, "oppositeDirection" : true, "depth" : 14.86 * mm, "offsetDistance" : 25.4 * mm});
        }
        {
            var Q0;
            Q0=makeQuery(id+"F30.boolean.opBoolean","COPY",FACE,{"derivedFrom":makeQuery(id+"F30.opExtrude","SWEPT_FACE",FACE,{"disambiguationData":[OSD([sQuery(id+"F29.wireOp",EDGE,"E109")])]})});
            var sketch = newSketch(context, id + "F31", { "sketchPlane" : qUnion([Q0])});
            skLineSegment(sketch, "E111", {"start": v(-25.02, 1.64) * mm, "end": v(-32.53, 1.64) * mm});
            skLineSegment(sketch, "E112", {"start": v(-32.53, 1.64) * mm, "end": v(-32.53, 0) * mm});
            skLineSegment(sketch, "E113", {"start": v(-32.53, 0) * mm, "end": v(-25.02, 0) * mm});
            skLineSegment(sketch, "E114", {"start": v(-25.02, 0) * mm, "end": v(-25.02, 1.64) * mm});
            skSolve(sketch);
        }
        {
            var Q0;
            Q0 = qSketchRegion(id + "F31", true);
            extrude(context, id + "F32", {"entities" : qUnion([Q0]), "depth" : 1.22 * mm, "offsetDistance" : 25.4 * mm});
        }
        {
            var Q0;
            Q0=makeQuery(id+"F1.opExtrude","SWEPT_FACE",FACE,{"disambiguationData":[OSD([sQuery(id+"F0.wireOp",EDGE,"E34")])]});
            var sketch = newSketch(context, id + "F33", { "sketchPlane" : qUnion([Q0])});
            skLineSegment(sketch, "E115", {"start": v(-19.24, 25.4) * mm, "end": v(1.64, 25.4) * mm});
            skLineSegment(sketch, "E116", {"start": v(1.64, 25.4) * mm, "end": v(1.64, 0) * mm});
            skLineSegment(sketch, "E117", {"start": v(1.64, 0) * mm, "end": v(-19.24, 0) * mm});
            skLineSegment(sketch, "E118", {"start": v(-19.24, 0) * mm, "end": v(-19.24, 25.4) * mm});
            skSolve(sketch);
        }
        {
            var Q0;
            Q0 = qSketchRegion(id + "F33", true);
            extrude(context, id + "F34", {"entities" : qUnion([Q0]), "operationType" : NewBodyOperationType.ADD, "depth" : 13.3 * mm, "offsetDistance" : 25.4 * mm});
        }
        {
            var Q0;
            Q0=makeQuery(id+"F1.opExtrude","SWEPT_FACE",FACE,{"disambiguationData":[OSD([sQuery(id+"F0.wireOp",EDGE,"E24"),sQuery(id+"F0.wireOp",EDGE,"E25"),sQuery(id+"F0.wireOp",EDGE,"E42")])]});
            var sketch = newSketch(context, id + "F35", { "sketchPlane" : qUnion([Q0])});
            skLineSegment(sketch, "E119", {"start": v(-17.73, 25.4) * mm, "end": v(-17.73, 0) * mm});
            skLineSegment(sketch, "E120", {"start": v(-25.02, 25.4) * mm, "end": v(-17.73, 25.4) * mm});
            skLineSegment(sketch, "E121", {"start": v(-25.02, 0) * mm, "end": v(-25.02, 25.4) * mm});
            skLineSegment(sketch, "E122", {"start": v(-17.73, 0) * mm, "end": v(-25.02, 0) * mm});
            skSolve(sketch);
        }
        {
            var Q0;
            Q0 = qSketchRegion(id + "F35", true);
            extrude(context, id + "F36", {"entities" : qUnion([Q0]), "operationType" : NewBodyOperationType.ADD, "depth" : 21.18 * mm, "offsetDistance" : 25.4 * mm});
        }
        {
            var Q0;
            {var subQ0=sQuery(id+"F0.wireOp",EDGE,"E58.7");var subQ1=sQuery(id+"F0.wireOp",EDGE,"E58.6");var subQ2=sQuery(id+"F0.wireOp",EDGE,"E58.5");var subQ3=sQuery(id+"F0.wireOp",EDGE,"E58.4");var subQ4=sQuery(id+"F0.wireOp",EDGE,"E58.3");var subQ5=sQuery(id+"F0.wireOp",EDGE,"E58.2");var subQ6=sQuery(id+"F0.wireOp",EDGE,"E58.1");var subQ7=sQuery(id+"F0.wireOp",EDGE,"E58.0");var subQ8=sQuery(id+"F0.wireOp",EDGE,"E55.7");var subQ9=sQuery(id+"F0.wireOp",EDGE,"E55.6");var subQ10=sQuery(id+"F0.wireOp",EDGE,"E55.5");var subQ11=sQuery(id+"F0.wireOp",EDGE,"E55.4");var subQ12=sQuery(id+"F0.wireOp",EDGE,"E55.3");var subQ13=sQuery(id+"F0.wireOp",EDGE,"E55.2");var subQ14=sQuery(id+"F0.wireOp",EDGE,"E55.1");var subQ15=sQuery(id+"F0.wireOp",EDGE,"E55.0");var subQ16=sQuery(id+"F0.wireOp",EDGE,"E53.3");var subQ17=sQuery(id+"F0.wireOp",EDGE,"E53.2");var subQ18=sQuery(id+"F0.wireOp",EDGE,"E53.1");var subQ19=sQuery(id+"F0.wireOp",EDGE,"E53.0");var subQ20=sQuery(id+"F0.wireOp",EDGE,"E52.5");var subQ21=sQuery(id+"F0.wireOp",EDGE,"E52.4");var subQ22=sQuery(id+"F0.wireOp",EDGE,"E52.3");var subQ23=sQuery(id+"F0.wireOp",EDGE,"E52.2");var subQ24=sQuery(id+"F0.wireOp",EDGE,"E52.1");var subQ25=sQuery(id+"F0.wireOp",EDGE,"E52.0");var subQ26=sQuery(id+"F0.wireOp",EDGE,"E65.0");var subQ27=sQuery(id+"F0.wireOp",EDGE,"E64");var subQ28=sQuery(id+"F0.wireOp",EDGE,"E63");var subQ29=sQuery(id+"F0.wireOp",EDGE,"E61.0");var subQ30=sQuery(id+"F0.wireOp",EDGE,"E60");var subQ31=sQuery(id+"F0.wireOp",EDGE,"E56.12");var subQ32=sQuery(id+"F0.wireOp",EDGE,"E56.11");var subQ33=sQuery(id+"F0.wireOp",EDGE,"E56.10");var subQ34=sQuery(id+"F0.wireOp",EDGE,"E56.9");var subQ35=sQuery(id+"F0.wireOp",EDGE,"E56.8");var subQ36=sQuery(id+"F0.wireOp",EDGE,"E56.7");var subQ37=sQuery(id+"F0.wireOp",EDGE,"E56.6");var subQ38=sQuery(id+"F0.wireOp",EDGE,"E56.5");var subQ39=sQuery(id+"F0.wireOp",EDGE,"E56.4");var subQ40=sQuery(id+"F0.wireOp",EDGE,"E56.3");var subQ41=sQuery(id+"F0.wireOp",EDGE,"E56.2");var subQ42=sQuery(id+"F0.wireOp",EDGE,"E56.1");var subQ43=sQuery(id+"F0.wireOp",EDGE,"E56.0");var subQ44=sQuery(id+"F0.wireOp",EDGE,"E50.8");var subQ45=sQuery(id+"F0.wireOp",EDGE,"E50.7");var subQ46=sQuery(id+"F0.wireOp",EDGE,"E50.6");var subQ47=sQuery(id+"F0.wireOp",EDGE,"E50.5");var subQ48=sQuery(id+"F0.wireOp",EDGE,"E50.4");var subQ49=sQuery(id+"F0.wireOp",EDGE,"E50.3");var subQ50=sQuery(id+"F0.wireOp",EDGE,"E50.2");var subQ51=sQuery(id+"F0.wireOp",EDGE,"E50.1");var subQ52=sQuery(id+"F0.wireOp",EDGE,"E50.0");var subQ53=sQuery(id+"F0.wireOp",EDGE,"E49");var subQ54=sQuery(id+"F0.wireOp",EDGE,"E48.4");var subQ55=sQuery(id+"F0.wireOp",EDGE,"E48.3");var subQ56=sQuery(id+"F0.wireOp",EDGE,"E48.2");var subQ57=sQuery(id+"F0.wireOp",EDGE,"E48.1");var subQ58=sQuery(id+"F0.wireOp",EDGE,"E48.0");var subQ59=sQuery(id+"F0.wireOp",EDGE,"E47");var subQ60=sQuery(id+"F0.wireOp",EDGE,"E46.3");var subQ61=sQuery(id+"F0.wireOp",EDGE,"E46.2");var subQ62=sQuery(id+"F0.wireOp",EDGE,"E46.1");var subQ63=sQuery(id+"F0.wireOp",EDGE,"E46.0");var subQ64=sQuery(id+"F0.wireOp",EDGE,"E7");var subQ65=sQuery(id+"F0.wireOp",EDGE,"E3");Q0=makeQuery(id+"F36.boolean.opBoolean","MERGE",FACE,{"derivedFrom":[makeQuery(id+"F34.boolean.opBoolean","MERGE",FACE,{"derivedFrom":[makeQuery(id+"F2.boolean.opBoolean","MERGE",FACE,{"derivedFrom":[makeQuery(id+"F1.opExtrude","CAP_FACE",FACE,{"disambiguationData":[OSD([sQuery(id+"F0.wireOp",EDGE,"E0"),sQuery(id+"F0.wireOp",EDGE,"E1"),sQuery(id+"F0.wireOp",EDGE,"E2"),subQ65,sQuery(id+"F0.wireOp",EDGE,"E4"),sQuery(id+"F0.wireOp",EDGE,"E5"),sQuery(id+"F0.wireOp",EDGE,"E6"),subQ64,sQuery(id+"F0.wireOp",EDGE,"E8"),sQuery(id+"F0.wireOp",EDGE,"E9"),sQuery(id+"F0.wireOp",EDGE,"E10"),sQuery(id+"F0.wireOp",EDGE,"E11"),sQuery(id+"F0.wireOp",EDGE,"E12"),sQuery(id+"F0.wireOp",EDGE,"E13"),sQuery(id+"F0.wireOp",EDGE,"E14"),sQuery(id+"F0.wireOp",EDGE,"E19"),sQuery(id+"F0.wireOp",EDGE,"E21"),sQuery(id+"F0.wireOp",EDGE,"E23"),sQuery(id+"F0.wireOp",EDGE,"E24"),sQuery(id+"F0.wireOp",EDGE,"E25"),sQuery(id+"F0.wireOp",EDGE,"E26"),sQuery(id+"F0.wireOp",EDGE,"E27"),sQuery(id+"F0.wireOp",EDGE,"E30"),sQuery(id+"F0.wireOp",EDGE,"E31"),sQuery(id+"F0.wireOp",EDGE,"E32"),sQuery(id+"F0.wireOp",EDGE,"E34"),sQuery(id+"F0.wireOp",EDGE,"E35"),sQuery(id+"F0.wireOp",EDGE,"E36"),sQuery(id+"F0.wireOp",EDGE,"E37"),sQuery(id+"F0.wireOp",EDGE,"E42"),sQuery(id+"F0.wireOp",EDGE,"E43"),sQuery(id+"F0.wireOp",EDGE,"E44"),sQuery(id+"F0.wireOp",EDGE,"E45"),subQ63,subQ62,subQ61,subQ60,subQ59,subQ58,subQ57,subQ56,subQ55,subQ54,subQ53,subQ52,subQ51,subQ50,subQ49,subQ48,subQ47,subQ46,subQ45,subQ44,subQ25,subQ24,subQ23,subQ22,subQ21,subQ20,subQ19,subQ18,subQ17,subQ16,sQuery(id+"F0.wireOp",EDGE,"E54"),subQ15,subQ14,subQ13,subQ12,subQ11,subQ10,subQ9,subQ8,subQ43,subQ42,subQ41,subQ40,subQ39,subQ38,subQ37,subQ36,subQ35,subQ34,subQ33,subQ32,subQ31,subQ7,subQ6,subQ5,subQ4,subQ3,subQ2,subQ1,subQ0,sQuery(id+"F0.wireOp",EDGE,"E59"),subQ30,subQ29,subQ28,subQ27,subQ26])],"isStart":true}),makeQuery(id+"F2.opExtrude","CAP_FACE",FACE,{"disambiguationData":[OSD([subQ65,subQ64,subQ63,subQ62,subQ61,subQ60,subQ59,subQ58,subQ57,subQ56,subQ55,subQ54,subQ53,subQ52,subQ51,subQ50,subQ49,subQ48,subQ47,subQ46,subQ45,subQ44,subQ43,subQ42,subQ41,subQ40,subQ39,subQ38,subQ37,subQ36,subQ35,subQ34,subQ33,subQ32,subQ31,subQ30,subQ29,subQ28,subQ27,subQ26])],"isStart":true}),makeQuery(id+"F2.opExtrude","CAP_FACE",FACE,{"disambiguationData":[OSD([subQ25,subQ24,subQ23,subQ22,subQ21,subQ20])],"isStart":true}),makeQuery(id+"F2.opExtrude","CAP_FACE",FACE,{"disambiguationData":[OSD([subQ19,subQ18,subQ17,subQ16])],"isStart":true}),makeQuery(id+"F2.opExtrude","CAP_FACE",FACE,{"disambiguationData":[OSD([subQ15,subQ14,subQ13,subQ12,subQ11,subQ10,subQ9,subQ8])],"isStart":true}),makeQuery(id+"F2.opExtrude","CAP_FACE",FACE,{"disambiguationData":[OSD([subQ7,subQ6,subQ5,subQ4,subQ3,subQ2,subQ1,subQ0])],"isStart":true})]}),makeQuery(id+"F34.opExtrude","SWEPT_FACE",FACE,{"disambiguationData":[OSD([sQuery(id+"F33.wireOp",EDGE,"E117")])]})]}),makeQuery(id+"F36.opExtrude","SWEPT_FACE",FACE,{"disambiguationData":[OSD([sQuery(id+"F35.wireOp",EDGE,"E122")])]})]});}
            var sketch = newSketch(context, id + "F37", { "sketchPlane" : qUnion([Q0])});
            skLineSegment(sketch, "E123", {"start": v(-25.02, 19.55) * mm, "end": v(-25.02, 0) * mm});
            skLineSegment(sketch, "E124", {"start": v(-25.02, 0) * mm, "end": v(-17.73, 0) * mm});
            skLineSegment(sketch, "E125", {"start": v(-17.73, 0) * mm, "end": v(-17.73, 19.55) * mm});
            skLineSegment(sketch, "E126", {"start": v(-17.73, 19.55) * mm, "end": v(-25.02, 19.55) * mm});
            skSolve(sketch);
        }
        {
            var Q0;
            Q0 = qSketchRegion(id + "F37", true);
            extrude(context, id + "F38", {"entities" : qUnion([Q0]), "depth" : 10.7 * mm, "offsetDistance" : 25.4 * mm});
        }
        {
            var Q0;
            Q0=makeQuery(id+"F38.opExtrude","SWEPT_FACE",FACE,{"disambiguationData":[OSD([sQuery(id+"F37.wireOp",EDGE,"E124")])]});
            var sketch = newSketch(context, id + "F39", { "sketchPlane" : qUnion([Q0])});
            skLineSegment(sketch, "E127", {"start": v(17.73, -10.7) * mm, "end": v(17.73, 0) * mm});
            skLineSegment(sketch, "E128", {"start": v(17.73, 0) * mm, "end": v(25.02, 0) * mm});
            skLineSegment(sketch, "E129", {"start": v(25.02, 0) * mm, "end": v(25.02, -10.7) * mm});
            skLineSegment(sketch, "E130", {"start": v(25.02, -10.7) * mm, "end": v(17.73, -10.7) * mm});
            skSolve(sketch);
        }
        {
            var Q0;
            Q0 = qSketchRegion(id + "F39", true);
            extrude(context, id + "F40", {"entities" : qUnion([Q0]), "depth" : 1.63 * mm, "offsetDistance" : 25.4 * mm});
        }
        {
            var Q0;
            {var subQ0=sQuery(id+"F0.wireOp",EDGE,"E58.7");var subQ1=sQuery(id+"F0.wireOp",EDGE,"E58.6");var subQ2=sQuery(id+"F0.wireOp",EDGE,"E58.5");var subQ3=sQuery(id+"F0.wireOp",EDGE,"E58.4");var subQ4=sQuery(id+"F0.wireOp",EDGE,"E58.3");var subQ5=sQuery(id+"F0.wireOp",EDGE,"E58.2");var subQ6=sQuery(id+"F0.wireOp",EDGE,"E58.1");var subQ7=sQuery(id+"F0.wireOp",EDGE,"E58.0");var subQ8=sQuery(id+"F0.wireOp",EDGE,"E55.7");var subQ9=sQuery(id+"F0.wireOp",EDGE,"E55.6");var subQ10=sQuery(id+"F0.wireOp",EDGE,"E55.5");var subQ11=sQuery(id+"F0.wireOp",EDGE,"E55.4");var subQ12=sQuery(id+"F0.wireOp",EDGE,"E55.3");var subQ13=sQuery(id+"F0.wireOp",EDGE,"E55.2");var subQ14=sQuery(id+"F0.wireOp",EDGE,"E55.1");var subQ15=sQuery(id+"F0.wireOp",EDGE,"E55.0");var subQ16=sQuery(id+"F0.wireOp",EDGE,"E53.3");var subQ17=sQuery(id+"F0.wireOp",EDGE,"E53.2");var subQ18=sQuery(id+"F0.wireOp",EDGE,"E53.1");var subQ19=sQuery(id+"F0.wireOp",EDGE,"E53.0");var subQ20=sQuery(id+"F0.wireOp",EDGE,"E52.5");var subQ21=sQuery(id+"F0.wireOp",EDGE,"E52.4");var subQ22=sQuery(id+"F0.wireOp",EDGE,"E52.3");var subQ23=sQuery(id+"F0.wireOp",EDGE,"E52.2");var subQ24=sQuery(id+"F0.wireOp",EDGE,"E52.1");var subQ25=sQuery(id+"F0.wireOp",EDGE,"E52.0");var subQ26=sQuery(id+"F0.wireOp",EDGE,"E65.0");var subQ27=sQuery(id+"F0.wireOp",EDGE,"E64");var subQ28=sQuery(id+"F0.wireOp",EDGE,"E63");var subQ29=sQuery(id+"F0.wireOp",EDGE,"E61.0");var subQ30=sQuery(id+"F0.wireOp",EDGE,"E60");var subQ31=sQuery(id+"F0.wireOp",EDGE,"E56.12");var subQ32=sQuery(id+"F0.wireOp",EDGE,"E56.11");var subQ33=sQuery(id+"F0.wireOp",EDGE,"E56.10");var subQ34=sQuery(id+"F0.wireOp",EDGE,"E56.9");var subQ35=sQuery(id+"F0.wireOp",EDGE,"E56.8");var subQ36=sQuery(id+"F0.wireOp",EDGE,"E56.7");var subQ37=sQuery(id+"F0.wireOp",EDGE,"E56.6");var subQ38=sQuery(id+"F0.wireOp",EDGE,"E56.5");var subQ39=sQuery(id+"F0.wireOp",EDGE,"E56.4");var subQ40=sQuery(id+"F0.wireOp",EDGE,"E56.3");var subQ41=sQuery(id+"F0.wireOp",EDGE,"E56.2");var subQ42=sQuery(id+"F0.wireOp",EDGE,"E56.1");var subQ43=sQuery(id+"F0.wireOp",EDGE,"E56.0");var subQ44=sQuery(id+"F0.wireOp",EDGE,"E50.8");var subQ45=sQuery(id+"F0.wireOp",EDGE,"E50.7");var subQ46=sQuery(id+"F0.wireOp",EDGE,"E50.6");var subQ47=sQuery(id+"F0.wireOp",EDGE,"E50.5");var subQ48=sQuery(id+"F0.wireOp",EDGE,"E50.4");var subQ49=sQuery(id+"F0.wireOp",EDGE,"E50.3");var subQ50=sQuery(id+"F0.wireOp",EDGE,"E50.2");var subQ51=sQuery(id+"F0.wireOp",EDGE,"E50.1");var subQ52=sQuery(id+"F0.wireOp",EDGE,"E50.0");var subQ53=sQuery(id+"F0.wireOp",EDGE,"E49");var subQ54=sQuery(id+"F0.wireOp",EDGE,"E48.4");var subQ55=sQuery(id+"F0.wireOp",EDGE,"E48.3");var subQ56=sQuery(id+"F0.wireOp",EDGE,"E48.2");var subQ57=sQuery(id+"F0.wireOp",EDGE,"E48.1");var subQ58=sQuery(id+"F0.wireOp",EDGE,"E48.0");var subQ59=sQuery(id+"F0.wireOp",EDGE,"E47");var subQ60=sQuery(id+"F0.wireOp",EDGE,"E46.3");var subQ61=sQuery(id+"F0.wireOp",EDGE,"E46.2");var subQ62=sQuery(id+"F0.wireOp",EDGE,"E46.1");var subQ63=sQuery(id+"F0.wireOp",EDGE,"E46.0");var subQ64=sQuery(id+"F0.wireOp",EDGE,"E7");var subQ65=sQuery(id+"F0.wireOp",EDGE,"E3");Q0=makeQuery(id+"F36.boolean.opBoolean","MERGE",FACE,{"derivedFrom":[makeQuery(id+"F34.boolean.opBoolean","MERGE",FACE,{"derivedFrom":[makeQuery(id+"F2.boolean.opBoolean","MERGE",FACE,{"derivedFrom":[makeQuery(id+"F1.opExtrude","CAP_FACE",FACE,{"disambiguationData":[OSD([sQuery(id+"F0.wireOp",EDGE,"E0"),sQuery(id+"F0.wireOp",EDGE,"E1"),sQuery(id+"F0.wireOp",EDGE,"E2"),subQ65,sQuery(id+"F0.wireOp",EDGE,"E4"),sQuery(id+"F0.wireOp",EDGE,"E5"),sQuery(id+"F0.wireOp",EDGE,"E6"),subQ64,sQuery(id+"F0.wireOp",EDGE,"E8"),sQuery(id+"F0.wireOp",EDGE,"E9"),sQuery(id+"F0.wireOp",EDGE,"E10"),sQuery(id+"F0.wireOp",EDGE,"E11"),sQuery(id+"F0.wireOp",EDGE,"E12"),sQuery(id+"F0.wireOp",EDGE,"E13"),sQuery(id+"F0.wireOp",EDGE,"E14"),sQuery(id+"F0.wireOp",EDGE,"E19"),sQuery(id+"F0.wireOp",EDGE,"E21"),sQuery(id+"F0.wireOp",EDGE,"E23"),sQuery(id+"F0.wireOp",EDGE,"E24"),sQuery(id+"F0.wireOp",EDGE,"E25"),sQuery(id+"F0.wireOp",EDGE,"E26"),sQuery(id+"F0.wireOp",EDGE,"E27"),sQuery(id+"F0.wireOp",EDGE,"E30"),sQuery(id+"F0.wireOp",EDGE,"E31"),sQuery(id+"F0.wireOp",EDGE,"E32"),sQuery(id+"F0.wireOp",EDGE,"E34"),sQuery(id+"F0.wireOp",EDGE,"E35"),sQuery(id+"F0.wireOp",EDGE,"E36"),sQuery(id+"F0.wireOp",EDGE,"E37"),sQuery(id+"F0.wireOp",EDGE,"E42"),sQuery(id+"F0.wireOp",EDGE,"E43"),sQuery(id+"F0.wireOp",EDGE,"E44"),sQuery(id+"F0.wireOp",EDGE,"E45"),subQ63,subQ62,subQ61,subQ60,subQ59,subQ58,subQ57,subQ56,subQ55,subQ54,subQ53,subQ52,subQ51,subQ50,subQ49,subQ48,subQ47,subQ46,subQ45,subQ44,subQ25,subQ24,subQ23,subQ22,subQ21,subQ20,subQ19,subQ18,subQ17,subQ16,sQuery(id+"F0.wireOp",EDGE,"E54"),subQ15,subQ14,subQ13,subQ12,subQ11,subQ10,subQ9,subQ8,subQ43,subQ42,subQ41,subQ40,subQ39,subQ38,subQ37,subQ36,subQ35,subQ34,subQ33,subQ32,subQ31,subQ7,subQ6,subQ5,subQ4,subQ3,subQ2,subQ1,subQ0,sQuery(id+"F0.wireOp",EDGE,"E59"),subQ30,subQ29,subQ28,subQ27,subQ26])],"isStart":true}),makeQuery(id+"F2.opExtrude","CAP_FACE",FACE,{"disambiguationData":[OSD([subQ65,subQ64,subQ63,subQ62,subQ61,subQ60,subQ59,subQ58,subQ57,subQ56,subQ55,subQ54,subQ53,subQ52,subQ51,subQ50,subQ49,subQ48,subQ47,subQ46,subQ45,subQ44,subQ43,subQ42,subQ41,subQ40,subQ39,subQ38,subQ37,subQ36,subQ35,subQ34,subQ33,subQ32,subQ31,subQ30,subQ29,subQ28,subQ27,subQ26])],"isStart":true}),makeQuery(id+"F2.opExtrude","CAP_FACE",FACE,{"disambiguationData":[OSD([subQ25,subQ24,subQ23,subQ22,subQ21,subQ20])],"isStart":true}),makeQuery(id+"F2.opExtrude","CAP_FACE",FACE,{"disambiguationData":[OSD([subQ19,subQ18,subQ17,subQ16])],"isStart":true}),makeQuery(id+"F2.opExtrude","CAP_FACE",FACE,{"disambiguationData":[OSD([subQ15,subQ14,subQ13,subQ12,subQ11,subQ10,subQ9,subQ8])],"isStart":true}),makeQuery(id+"F2.opExtrude","CAP_FACE",FACE,{"disambiguationData":[OSD([subQ7,subQ6,subQ5,subQ4,subQ3,subQ2,subQ1,subQ0])],"isStart":true})]}),makeQuery(id+"F34.opExtrude","SWEPT_FACE",FACE,{"disambiguationData":[OSD([sQuery(id+"F33.wireOp",EDGE,"E117")])]})]}),makeQuery(id+"F36.opExtrude","SWEPT_FACE",FACE,{"disambiguationData":[OSD([sQuery(id+"F35.wireOp",EDGE,"E122")])]})]});}
            var sketch = newSketch(context, id + "F41", { "sketchPlane" : qUnion([Q0])});
            skLineSegment(sketch, "E131", {"start": v(-36.9, 19.24) * mm, "end": v(-36.9, -1.64) * mm});
            skLineSegment(sketch, "E132", {"start": v(-36.9, -1.64) * mm, "end": v(-32.55, -1.64) * mm});
            skLineSegment(sketch, "E133", {"start": v(-32.55, -1.64) * mm, "end": v(-32.55, 19.24) * mm});
            skLineSegment(sketch, "E134", {"start": v(-32.55, 19.24) * mm, "end": v(-36.9, 19.24) * mm});
            skSolve(sketch);
        }
        {
            var Q0;
            Q0 = qSketchRegion(id + "F41", true);
            extrude(context, id + "F42", {"entities" : qUnion([Q0]), "operationType" : NewBodyOperationType.ADD, "depth" : 10.7 * mm, "offsetDistance" : 25.4 * mm});
        }
        {
            var Q0;
            Q0=makeQuery(id+"F1.opExtrude","SWEPT_FACE",FACE,{"disambiguationData":[OSD([sQuery(id+"F0.wireOp",EDGE,"E12")])]});
            var sketch = newSketch(context, id + "F43", { "sketchPlane" : qUnion([Q0])});
            skLineSegment(sketch, "E135", {"start": v(-28.95, 25.4) * mm, "end": v(-28.95, 0) * mm});
            skLineSegment(sketch, "E136", {"start": v(-28.95, 0) * mm, "end": v(-17.16, 0) * mm});
            skLineSegment(sketch, "E137", {"start": v(-17.16, 0) * mm, "end": v(-17.05, 25.4) * mm});
            skLineSegment(sketch, "E138", {"start": v(-17.05, 25.4) * mm, "end": v(-28.95, 25.4) * mm});
            skSolve(sketch);
        }
        {
            var Q0;
            Q0 = qSketchRegion(id + "F43", true);
            extrude(context, id + "F44", {"entities" : qUnion([Q0]), "operationType" : NewBodyOperationType.ADD, "depth" : 13.44 * mm, "offsetDistance" : 25.4 * mm});
        }
        {
            var Q0;
            Q0=makeQuery(id+"F1.opExtrude","SWEPT_FACE",FACE,{"disambiguationData":[OSD([sQuery(id+"F0.wireOp",EDGE,"E50.8")])]});
            var sketch = newSketch(context, id + "F45", { "sketchPlane" : qUnion([Q0])});
            skLineSegment(sketch, "E139", {"start": v(12.59, 25.4) * mm, "end": v(24.38, 25.4) * mm});
            skLineSegment(sketch, "E140", {"start": v(24.38, 25.4) * mm, "end": v(24.38, 0.25) * mm});
            skLineSegment(sketch, "E141", {"start": v(24.38, 0.25) * mm, "end": v(12.59, 0.25) * mm});
            skLineSegment(sketch, "E142", {"start": v(12.59, 0.25) * mm, "end": v(12.59, 25.4) * mm});
            skSolve(sketch);
        }
        {
            var Q0;
            Q0=makeQuery(id+"F45.imprint","IMPRINT",FACE,{"disambiguationData":[TD([[makeQuery(id+"F45.imprint","IMPRINT",EDGE,{"derivedFrom":sQuery(id+"F45.wireOp",EDGE,"E139")}),1.0]])]});
            extrude(context, id + "F46", {"entities" : qUnion([Q0]), "operationType" : NewBodyOperationType.REMOVE, "oppositeDirection" : true, "depth" : 15.24 * mm, "offsetDistance" : 25.4 * mm});
        }
        {
            var Q0;
            Q0=makeQuery(id+"F42.boolean.opBoolean","MERGE",FACE,{"derivedFrom":[makeQuery(id+"F34.opExtrude","SWEPT_FACE",FACE,{"disambiguationData":[OSD([sQuery(id+"F33.wireOp",EDGE,"E118")])]}),makeQuery(id+"F42.opExtrude","SWEPT_FACE",FACE,{"disambiguationData":[OSD([sQuery(id+"F41.wireOp",EDGE,"E134")])]})]});
            var sketch = newSketch(context, id + "F47", { "sketchPlane" : qUnion([Q0])});
            skLineSegment(sketch, "E143", {"start": v(-32.55, 25.4) * mm, "end": v(-32.55, -10.7) * mm});
            skLineSegment(sketch, "E144", {"start": v(-32.55, -10.7) * mm, "end": v(-36.9, -10.7) * mm});
            skLineSegment(sketch, "E145", {"start": v(-36.9, -10.7) * mm, "end": v(-36.9, 25.4) * mm});
            skLineSegment(sketch, "E146", {"start": v(-36.9, 25.4) * mm, "end": v(-32.55, 25.4) * mm});
            skSolve(sketch);
        }
        {
            var Q0;
            Q0 = qSketchRegion(id + "F47", true);
            extrude(context, id + "F48", {"entities" : qUnion([Q0]), "operationType" : NewBodyOperationType.ADD, "depth" : 8.2 * mm, "offsetDistance" : 25.4 * mm});
        }
        {
            var Q0;
            Q0=makeQuery(id+"F48.boolean.opBoolean","MERGE",FACE,{"derivedFrom":[makeQuery(id+"F42.boolean.opBoolean","MERGE",FACE,{"derivedFrom":[makeQuery(id+"F34.opExtrude","CAP_FACE",FACE,{"disambiguationData":[OSD([sQuery(id+"F33.wireOp",EDGE,"E115"),sQuery(id+"F33.wireOp",EDGE,"E116"),sQuery(id+"F33.wireOp",EDGE,"E117"),sQuery(id+"F33.wireOp",EDGE,"E118")])],"isStart":false}),makeQuery(id+"F42.opExtrude","SWEPT_FACE",FACE,{"disambiguationData":[OSD([sQuery(id+"F41.wireOp",EDGE,"E133")])]})]}),makeQuery(id+"F48.opExtrude","SWEPT_FACE",FACE,{"disambiguationData":[OSD([sQuery(id+"F47.wireOp",EDGE,"E143")])]})]});
            var sketch = newSketch(context, id + "F49", { "sketchPlane" : qUnion([Q0])});
            skLineSegment(sketch, "E147", {"start": v(-27.43, -10.7) * mm, "end": v(-27.43, 25.4) * mm});
            skLineSegment(sketch, "E148", {"start": v(-27.43, 25.4) * mm, "end": v(-17.93, 25.4) * mm});
            skLineSegment(sketch, "E149", {"start": v(-17.93, 25.4) * mm, "end": v(-17.93, -10.7) * mm});
            skLineSegment(sketch, "E150", {"start": v(-17.93, -10.7) * mm, "end": v(-27.43, -10.7) * mm});
            skSolve(sketch);
        }
        {
            var Q0;
            Q0 = qSketchRegion(id + "F49", true);
            extrude(context, id + "F50", {"entities" : qUnion([Q0]), "depth" : 15.67 * mm, "offsetDistance" : 25.4 * mm});
        }
    });
